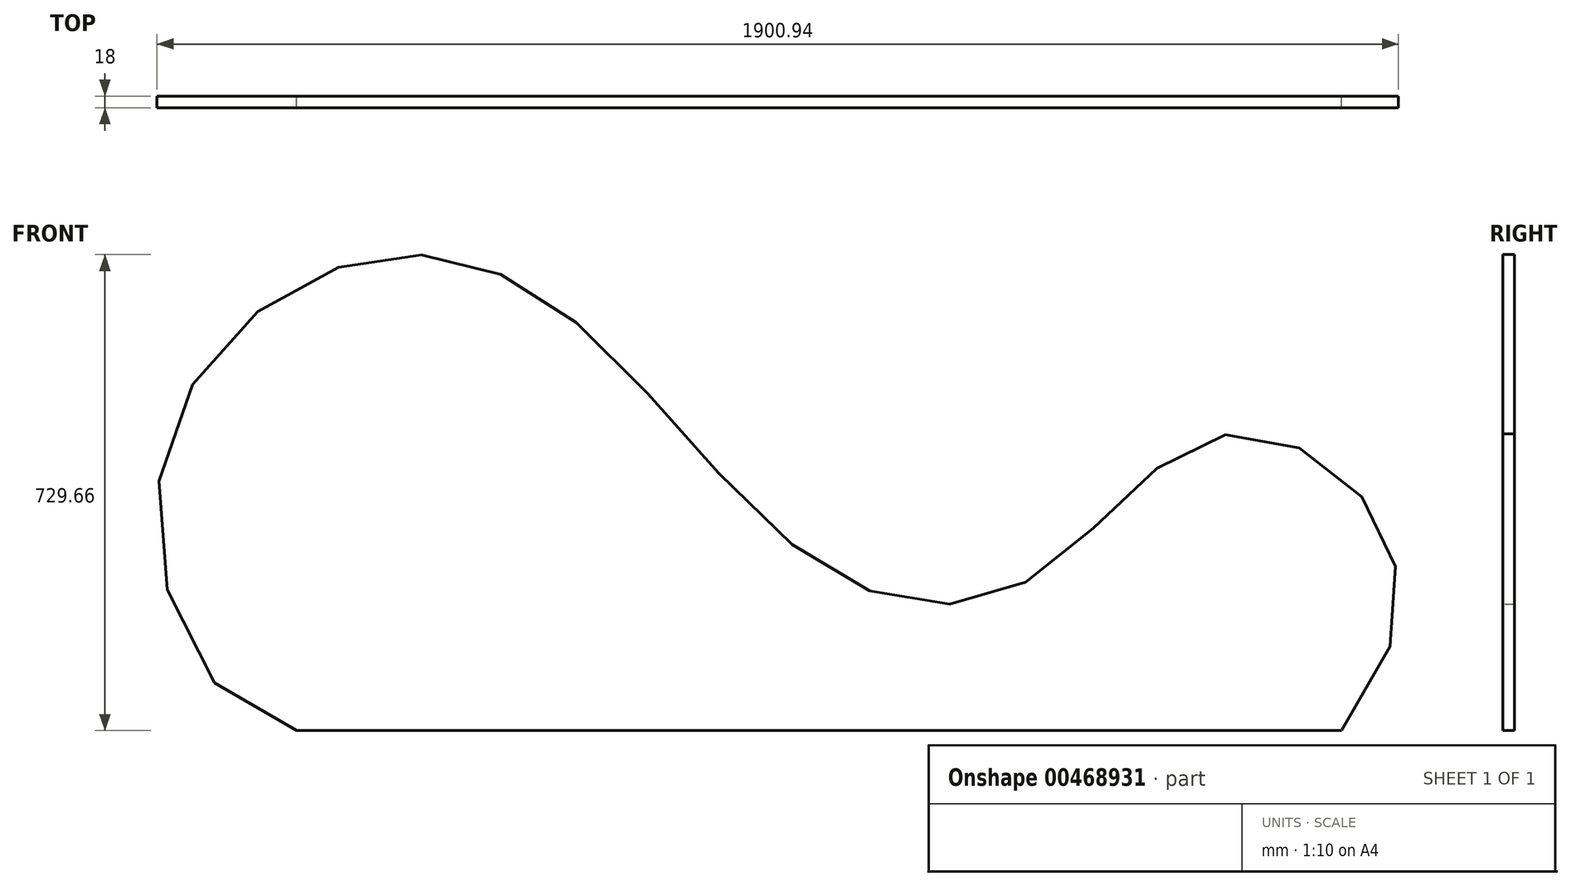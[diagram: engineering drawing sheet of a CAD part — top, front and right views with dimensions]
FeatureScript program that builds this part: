
annotation { "Feature Type Name" : "Feature", "Feature Type Description" : "" }
export const myFeature = defineFeature(function(context is Context, id is Id, definition is map)
    precondition{}
    {
        {
            var Q0;
            Q0=qCreatedBy(makeId("Front.planeOp"),FACE);
            var sketch = newSketch(context, id + "F0", { "sketchPlane" : qUnion([Q0])});
            skFitSpline(sketch, "E0", {"points": [v(-875.08, -507.13) * mm, v(-1081.7, -97.46) * mm, v(-778.87, 212.87) * mm, v(-448.5, 119.11) * mm, v(-68.59, -257.13) * mm, v(245.26, -277.32) * mm, v(529.74, -57.13) * mm, v(777.51, -178.21) * mm, v(724.92, -507.13) * mm], "startDerivative": vector(-3456.1, 547.05) * mm, "endDerivative": vector(-2532.15, -2951.5) * mm});
            skLineSegment(sketch, "E1", {"start": v(-875.08, -507.13) * mm, "end": v(724.92, -507.13) * mm});
            skSolve(sketch);
        }
        {
            var Q0;
            Q0 = qSketchRegion(id + "F0", true);
            extrude(context, id + "F1", {"entities" : qUnion([Q0]), "offsetDistance" : 25 * mm, "depth" : 18 * mm});
        }
    });
